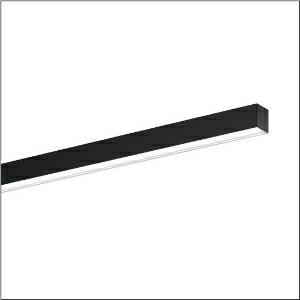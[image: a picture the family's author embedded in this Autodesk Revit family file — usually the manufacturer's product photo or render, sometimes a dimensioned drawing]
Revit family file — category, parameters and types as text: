
# Revit family: silica_21_51mx23tbt5b
name_source: partatom
category: Lighting Fixtures
units: mm (PartAtom-declared; Revit-internal decimal feet)

## family parameters
Cut with Voids When Loaded = No
Host = Face
Light Source = No
Part Type = Normal
Room Calculation Point = No
Round Connector Dimension = Use Diameter
Shared = No

## types (1)
- --- (1 x LED, 4030 lm, 40.5 W, 6500K)
    Apparent Load = 41 VA
    CIE Flux Codes = 78 96 99 100 100
    Color Rendering = 80
    Color Temperature = 6500K
    Default Elevation = 1800 mm
    Description = Silica 21, office luminaire, primary optical cover: prismatic diffuser, of PMMA, CAT 2 (L<= 3000cd/m²), light emission: direct distribution, primary light characteristic: symmetric, installation type: surface-mounted, LED, rated luminous flux: 4.030lm, luminous efficacy: 95lm/W, light colour: 8tw, colour temperature: 2700..6500K, control gear: DALI DT8, with terminal, 3+2-pole, max. 2.5mm², mains connection: 220..240V, AC, 50/60Hz, rated input power: 42.6W, luminaire housing, of aluminium, matt jet black (RAL 9005), length: 1.504mm, width: 53mm, height: 53mm, protection rating (complete): IP20, insulation class (complete): insulation class I (protective earthing), certification: CE, permissible operating ambient temperature: 0..+35°C, standard: EN 50419, packaging unit: 1 piece
    Height = 53 mm
    Lamp = 1 x LED
    Lamp Light Flux = 4030 lm
    Lamp Power = 40.5 W
    Lamp count = 1
    Length = 1504 mm
    Luminous efficacy = 100 lm/W
    Manufacturer = Siteco
    ModVariant = No
    Model = 51MX23TBT5B
    Mounting Place = Ceiling
    Mounting Type = Surface mounted
    Number of Poles = 1
    OnlyDefault = Yes
    Power Factor = 1
    Product Name = Silica 21
    Product group = office luminaire | ceiling mounted
    ProductGroupID = 301
    Protection Class = Protection class I
    Protection Degree = IP 20
    RLX_Detail_Level = 1
    RLX_Emergency_Light_Flux = 0 lm
    RLX_Emergency_Type = 0
    RLX_Emergency_Type_DB = No
    RlxData = <blob elided: 20425 chars, md5=43c81606>
    Socket = socket
    Standby Power = 0 W
    System Light Flux = 4030 lm
    System Power = 41 W
    Type Comments = individual setting
    Type Image = l_1335925.jpg
    URL = http://relux.com
    VarID = @adj_139307
    Voltage = 0 V
    Weight = 0.00 kg
    Width = 53 mm

## geometry (parser evidence)
native form markers: Blend x4, Sweep x12
no freeform markers — native parametric forms only
